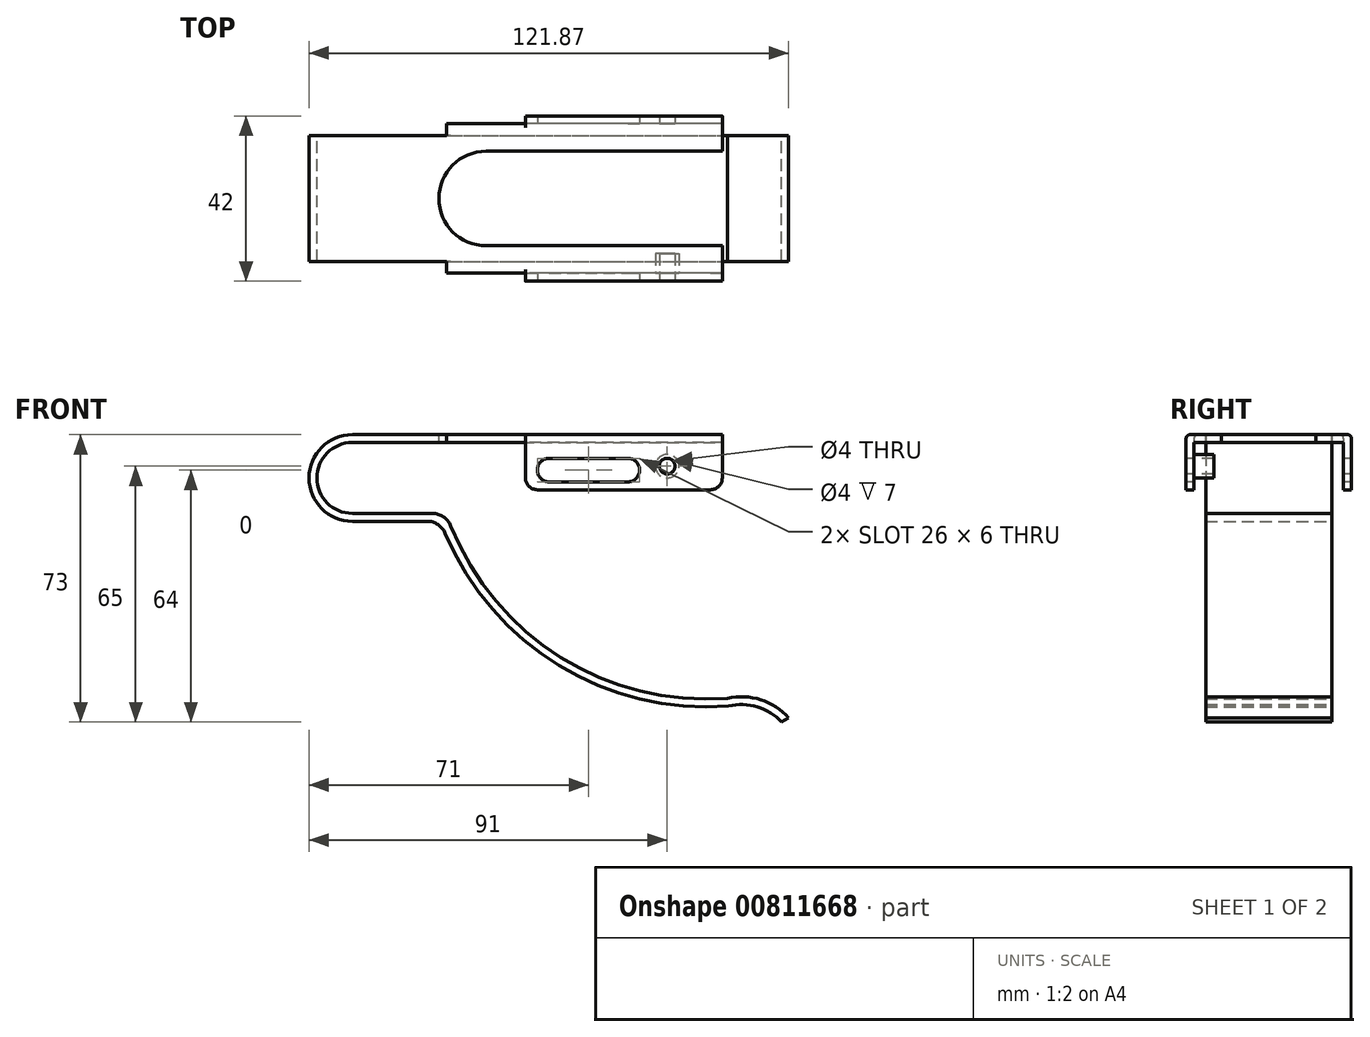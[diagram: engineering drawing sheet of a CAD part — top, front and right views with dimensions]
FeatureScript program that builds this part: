
annotation { "Feature Type Name" : "Feature", "Feature Type Description" : "" }
export const myFeature = defineFeature(function(context is Context, id is Id, definition is map)
    precondition{}
    {
        {
            var Q0;
            Q0=qCreatedBy(makeId("Front.planeOp"),FACE);
            var sketch = newSketch(context, id + "F0", { "sketchPlane" : qUnion([Q0])});
            skArc(sketch, "E0", {"start": v(0, 9) * mm, "mid": v(-9, 0) * mm, "end": v(0, -9) * mm});
            skLineSegment(sketch, "E1", {"start": v(0, 9) * mm, "end": v(94, 9) * mm});
            skLineSegment(sketch, "E2", {"start": v(0, -9) * mm, "end": v(20.34, -9) * mm});
            skArc(sketch, "E3", {"start": v(24.99, -12.15) * mm, "mid": v(52.96, -45.6) * mm, "end": v(95.3, -56) * mm});
            skArc(sketch, "E4", {"start": v(110.87, -61) * mm, "mid": v(103.77, -56.36) * mm, "end": v(95.3, -56) * mm});
            skPoint(sketch, "E5.visualSharp", {"position": v(23.82, -9) * mm});
            skArc(sketch, "E5.filletArc", {"start": v(24.99, -12.15) * mm, "mid": v(23.15, -9.86) * mm, "end": v(20.34, -9) * mm});
            skLineSegment(sketch, "E6.0", {"start": v(0, 11) * mm, "end": v(94, 11) * mm});
            skArc(sketch, "E6.1", {"start": v(109.07, -62) * mm, "mid": v(102.88, -58.18) * mm, "end": v(95.6, -57.98) * mm});
            skArc(sketch, "E6.2", {"start": v(23.61, -14.06) * mm, "mid": v(52.5, -47.67) * mm, "end": v(95.6, -57.98) * mm});
            skLineSegment(sketch, "E6.3", {"start": v(0, -11) * mm, "end": v(19, -11) * mm});
            skArc(sketch, "E6.4", {"start": v(0, 11) * mm, "mid": v(-11, 0) * mm, "end": v(0, -11) * mm});
            skPoint(sketch, "E7.visualSharp", {"position": v(22.4, -11) * mm});
            skArc(sketch, "E7.filletArc", {"start": v(23.61, -14.06) * mm, "mid": v(21.77, -11.84) * mm, "end": v(19, -11) * mm});
            skLineSegment(sketch, "E8", {"start": v(109.07, -62) * mm, "end": v(110.87, -61) * mm});
            skLineSegment(sketch, "E9", {"start": v(94, 9) * mm, "end": v(94, 11) * mm});
            skPoint(sketch, "E10", {"position": v(116.38, -61) * mm});
            skSolve(sketch);
        }
        {
            var Q0;
            Q0 = qSketchRegion(id + "F0", true);
            extrude(context, id + "F1", {"entities" : qUnion([Q0]), "depth" : 16 * mm, "offsetDistance" : 25 * mm});
        }
        {
            var Q0;
            Q0=makeQuery(id+"F1.opExtrude","SWEPT_FACE",FACE,{"disambiguationData":[OSD([sQuery(id+"F0.wireOp",EDGE,"E6.0")])]});
            var sketch = newSketch(context, id + "F2", { "sketchPlane" : qUnion([Q0])});
            skLineSegment(sketch, "E11.bottom", {"start": v(94, -16) * mm, "end": v(24, -16) * mm});
            skLineSegment(sketch, "E11.top", {"start": v(94, -19) * mm, "end": v(24, -19) * mm});
            skLineSegment(sketch, "E11.left", {"start": v(94, -16) * mm, "end": v(94, -19) * mm});
            skLineSegment(sketch, "E11.right", {"start": v(24, -16) * mm, "end": v(24, -19) * mm});
            skSolve(sketch);
        }
        {
            var Q0;
            Q0 = qSketchRegion(id + "F2", true);
            extrude(context, id + "F3", {"entities" : qUnion([Q0]), "operationType" : NewBodyOperationType.ADD, "oppositeDirection" : true, "depth" : 2 * mm, "offsetDistance" : 25 * mm});
        }
        {
            var Q0;
            Q0=makeQuery(id+"F3.opExtrude","SWEPT_FACE",FACE,{"disambiguationData":[OSD([sQuery(id+"F2.wireOp",EDGE,"E11.top")])]});
            var sketch = newSketch(context, id + "F4", { "sketchPlane" : qUnion([Q0])});
            skLineSegment(sketch, "E12.bottom", {"start": v(94, 11) * mm, "end": v(44, 11) * mm});
            skLineSegment(sketch, "E12.top", {"start": v(94, -3) * mm, "end": v(44, -3) * mm});
            skLineSegment(sketch, "E12.left", {"start": v(94, 11) * mm, "end": v(94, -3) * mm});
            skLineSegment(sketch, "E12.right", {"start": v(44, 11) * mm, "end": v(44, -3) * mm});
            skSolve(sketch);
        }
        {
            var Q0;
            Q0 = qSketchRegion(id + "F4", true);
            extrude(context, id + "F5", {"entities" : qUnion([Q0]), "operationType" : NewBodyOperationType.ADD, "depth" : 2 * mm, "offsetDistance" : 25 * mm});
        }
        {
            var Q0;
            Q0=makeQuery(id+"F5.opExtrude","CAP_EDGE",EDGE,{"disambiguationData":[OSD([sQuery(id+"F4.wireOp",EDGE,"E12.bottom")])],"isStart":false});
            var Q1;
            Q1=makeQuery(id+"F3.opExtrude","CAP_EDGE",EDGE,{"disambiguationData":[OSD([sQuery(id+"F2.wireOp",EDGE,"E11.top")])],"isStart":true});
            fillet(context, id + "F6", {"entities" : qUnion([Q0, Q1]), "radius" : 1 * mm, "tangentPropagation" : true, "allowEdgeOverflow" : false});
        }
        {
            var Q0;
            Q0=makeQuery(id+"F1.opExtrude","SWEPT_BODY",BODY,{"disambiguationData":[OSD([sQuery(id+"F0.wireOp",EDGE,"E0"),sQuery(id+"F0.wireOp",EDGE,"E1"),sQuery(id+"F0.wireOp",EDGE,"E2"),sQuery(id+"F0.wireOp",EDGE,"E3"),sQuery(id+"F0.wireOp",EDGE,"E4"),sQuery(id+"F0.wireOp",EDGE,"E5.filletArc"),sQuery(id+"F0.wireOp",EDGE,"E6.0"),sQuery(id+"F0.wireOp",EDGE,"E6.1"),sQuery(id+"F0.wireOp",EDGE,"E6.2"),sQuery(id+"F0.wireOp",EDGE,"E6.3"),sQuery(id+"F0.wireOp",EDGE,"E6.4"),sQuery(id+"F0.wireOp",EDGE,"E7.filletArc"),sQuery(id+"F0.wireOp",EDGE,"E8"),sQuery(id+"F0.wireOp",EDGE,"E9")])]});
            var Q1;
            Q1=qCreatedBy(makeId("Front.planeOp"),FACE);
            mirror(context, id + "F7", {"operationType" : NewBodyOperationType.ADD, "entities" : qUnion([Q0]), "mirrorPlane" : qUnion([Q1])});
        }
        {
            var Q0;
            {var subQ0=makeQuery(id+"F5.boolean.opBoolean","MERGE",FACE,{"derivedFrom":[makeQuery(id+"F3.boolean.opBoolean","MERGE",FACE,{"derivedFrom":[makeQuery(id+"F1.opExtrude","SWEPT_FACE",FACE,{"disambiguationData":[OSD([sQuery(id+"F0.wireOp",EDGE,"E6.0")])]}),makeQuery(id+"F3.opExtrude","CAP_FACE",FACE,{"disambiguationData":[OSD([sQuery(id+"F2.wireOp",EDGE,"E11.bottom"),sQuery(id+"F2.wireOp",EDGE,"E11.top"),sQuery(id+"F2.wireOp",EDGE,"E11.left"),sQuery(id+"F2.wireOp",EDGE,"E11.right")])],"isStart":true})]}),makeQuery(id+"F5.opExtrude","SWEPT_FACE",FACE,{"disambiguationData":[OSD([sQuery(id+"F4.wireOp",EDGE,"E12.bottom")])]})]});Q0=makeQuery(id+"F7.boolean.opBoolean","MERGE",FACE,{"derivedFrom":[subQ0,makeQuery(id+"F7.opPattern","COPY",FACE,{"derivedFrom":subQ0,"instanceName":"1"})]});}
            var sketch = newSketch(context, id + "F8", { "sketchPlane" : qUnion([Q0])});
            skArc(sketch, "E13", {"start": v(34, 12) * mm, "mid": v(22, 0) * mm, "end": v(34, -12) * mm});
            skLineSegment(sketch, "E14", {"start": v(34, -12) * mm, "end": v(94, -12) * mm});
            skLineSegment(sketch, "E15", {"start": v(34, 12) * mm, "end": v(94, 12) * mm});
            skSolve(sketch);
        }
        {
            var Q0;
            Q0 = qSketchRegion(id + "F8", true);
            var Q1;
            Q1=makeQuery(id+"F8.imprint","IMPRINT",FACE,{"disambiguationData":[TD([[makeQuery(id+"F8.imprint","IMPRINT",EDGE,{"derivedFrom":sQuery(id+"F8.wireOp",EDGE,"E13")}),1.0]])]});
            extrude(context, id + "F9", {"entities" : qUnion([Q0, Q1]), "operationType" : NewBodyOperationType.REMOVE, "oppositeDirection" : true, "depth" : 2 * mm, "offsetDistance" : 25 * mm});
        }
        {
            var Q0;
            Q0=makeQuery(id+"F5.opExtrude","CAP_FACE",FACE,{"disambiguationData":[OSD([sQuery(id+"F4.wireOp",EDGE,"E12.bottom"),sQuery(id+"F4.wireOp",EDGE,"E12.top"),sQuery(id+"F4.wireOp",EDGE,"E12.left"),sQuery(id+"F4.wireOp",EDGE,"E12.right")])],"isStart":false});
            var sketch = newSketch(context, id + "F10", { "sketchPlane" : qUnion([Q0])});
            skLineSegment(sketch, "E16", {"start": v(50, 2) * mm, "end": v(70, 2) * mm});
            skArc(sketch, "E17.0.startCap", {"start": v(50, -1) * mm, "mid": v(47, 2) * mm, "end": v(50, 5) * mm});
            skArc(sketch, "E17.0.endCap", {"start": v(70, 5) * mm, "mid": v(73, 2) * mm, "end": v(70, -1) * mm});
            skLineSegment(sketch, "E17.0.left", {"start": v(50, 5) * mm, "end": v(70, 5) * mm});
            skLineSegment(sketch, "E17.0.right", {"start": v(50, -1) * mm, "end": v(70, -1) * mm});
            skSolve(sketch);
        }
        {
            var Q0;
            Q0 = qSketchRegion(id + "F10", true);
            extrude(context, id + "F11", {"entities" : qUnion([Q0]), "operationType" : NewBodyOperationType.REMOVE, "endBound" : BoundingType.THROUGH_ALL, "oppositeDirection" : true, "depth" : 25 * mm, "offsetDistance" : 25 * mm});
        }
        {
            var Q0;
            Q0=makeQuery(id+"F5.opExtrude","CAP_FACE",FACE,{"disambiguationData":[OSD([sQuery(id+"F4.wireOp",EDGE,"E12.bottom"),sQuery(id+"F4.wireOp",EDGE,"E12.top"),sQuery(id+"F4.wireOp",EDGE,"E12.left"),sQuery(id+"F4.wireOp",EDGE,"E12.right")])],"isStart":false});
            var sketch = newSketch(context, id + "F12", { "sketchPlane" : qUnion([Q0])});
            skPoint(sketch, "E18", {"position": v(80, 3) * mm});
            skSolve(sketch);
        }
        {
            var Q0;
            Q0=sQuery(id+"F12.wireOp",VERTEX,"E18");
            var Q1;
            Q1=makeQuery(id+"F1.opExtrude","SWEPT_BODY",BODY,{"disambiguationData":[OSD([sQuery(id+"F0.wireOp",EDGE,"E0"),sQuery(id+"F0.wireOp",EDGE,"E1"),sQuery(id+"F0.wireOp",EDGE,"E2"),sQuery(id+"F0.wireOp",EDGE,"E3"),sQuery(id+"F0.wireOp",EDGE,"E4"),sQuery(id+"F0.wireOp",EDGE,"E5.filletArc"),sQuery(id+"F0.wireOp",EDGE,"E6.0"),sQuery(id+"F0.wireOp",EDGE,"E6.1"),sQuery(id+"F0.wireOp",EDGE,"E6.2"),sQuery(id+"F0.wireOp",EDGE,"E6.3"),sQuery(id+"F0.wireOp",EDGE,"E6.4"),sQuery(id+"F0.wireOp",EDGE,"E7.filletArc"),sQuery(id+"F0.wireOp",EDGE,"E8"),sQuery(id+"F0.wireOp",EDGE,"E9")])]});
            hole(context, id + "F13", {"style" : HoleStyle.SIMPLE, "endStyle" : HoleEndStyle.THROUGH, "holeDiameter" : 4 * mm, "majorDiameter" : 5 * mm, "isTappedThrough" : true, "tappedDepth" : 12 * mm, "tapClearance" : 3, "locations" : qUnion([Q0]), "scope" : qUnion([Q1])});
        }
        {
            var Q0;
            Q0=makeQuery(id+"F5.opExtrude","CAP_FACE",FACE,{"disambiguationData":[OSD([sQuery(id+"F4.wireOp",EDGE,"E12.bottom"),sQuery(id+"F4.wireOp",EDGE,"E12.top"),sQuery(id+"F4.wireOp",EDGE,"E12.left"),sQuery(id+"F4.wireOp",EDGE,"E12.right")])],"isStart":true});
            var sketch = newSketch(context, id + "F14", { "sketchPlane" : qUnion([Q0])});
            skCircle(sketch, "E19.0", {"center": v(-80, 3) * mm, "radius": 2 * mm});
            skCircle(sketch, "E20.0", {"center": v(-80, 3) * mm, "radius": 3 * mm});
            skSolve(sketch);
        }
        {
            var Q0;
            Q0 = qSketchRegion(id + "F14", true);
            extrude(context, id + "F15", {"entities" : qUnion([Q0]), "operationType" : NewBodyOperationType.ADD, "depth" : 5 * mm, "offsetDistance" : 25 * mm});
        }
        {
            var Q0;
            Q0=makeQuery(id+"F5.opExtrude","SWEPT_EDGE",EDGE,{"disambiguationData":[OSD([sQuery(id+"F4.wireOp",EDGE,"E12.top"),sQuery(id+"F4.wireOp",EDGE,"E12.right")])]});
            var Q1;
            Q1=makeQuery(id+"F5.opExtrude","SWEPT_EDGE",EDGE,{"disambiguationData":[OSD([sQuery(id+"F4.wireOp",EDGE,"E12.top"),sQuery(id+"F4.wireOp",EDGE,"E12.left")])]});
            var Q2;
            Q2=makeQuery(id+"F7.opPattern","COPY",EDGE,{"derivedFrom":makeQuery(id+"F5.opExtrude","SWEPT_EDGE",EDGE,{"disambiguationData":[OSD([sQuery(id+"F4.wireOp",EDGE,"E12.top"),sQuery(id+"F4.wireOp",EDGE,"E12.left")])]}),"instanceName":"1"});
            var Q3;
            Q3=makeQuery(id+"F7.opPattern","COPY",EDGE,{"derivedFrom":makeQuery(id+"F5.opExtrude","SWEPT_EDGE",EDGE,{"disambiguationData":[OSD([sQuery(id+"F4.wireOp",EDGE,"E12.top"),sQuery(id+"F4.wireOp",EDGE,"E12.right")])]}),"instanceName":"1"});
            fillet(context, id + "F16", {"entities" : qUnion([Q0, Q1, Q2, Q3]), "radius" : 3 * mm, "tangentPropagation" : true, "allowEdgeOverflow" : false});
        }
    });
